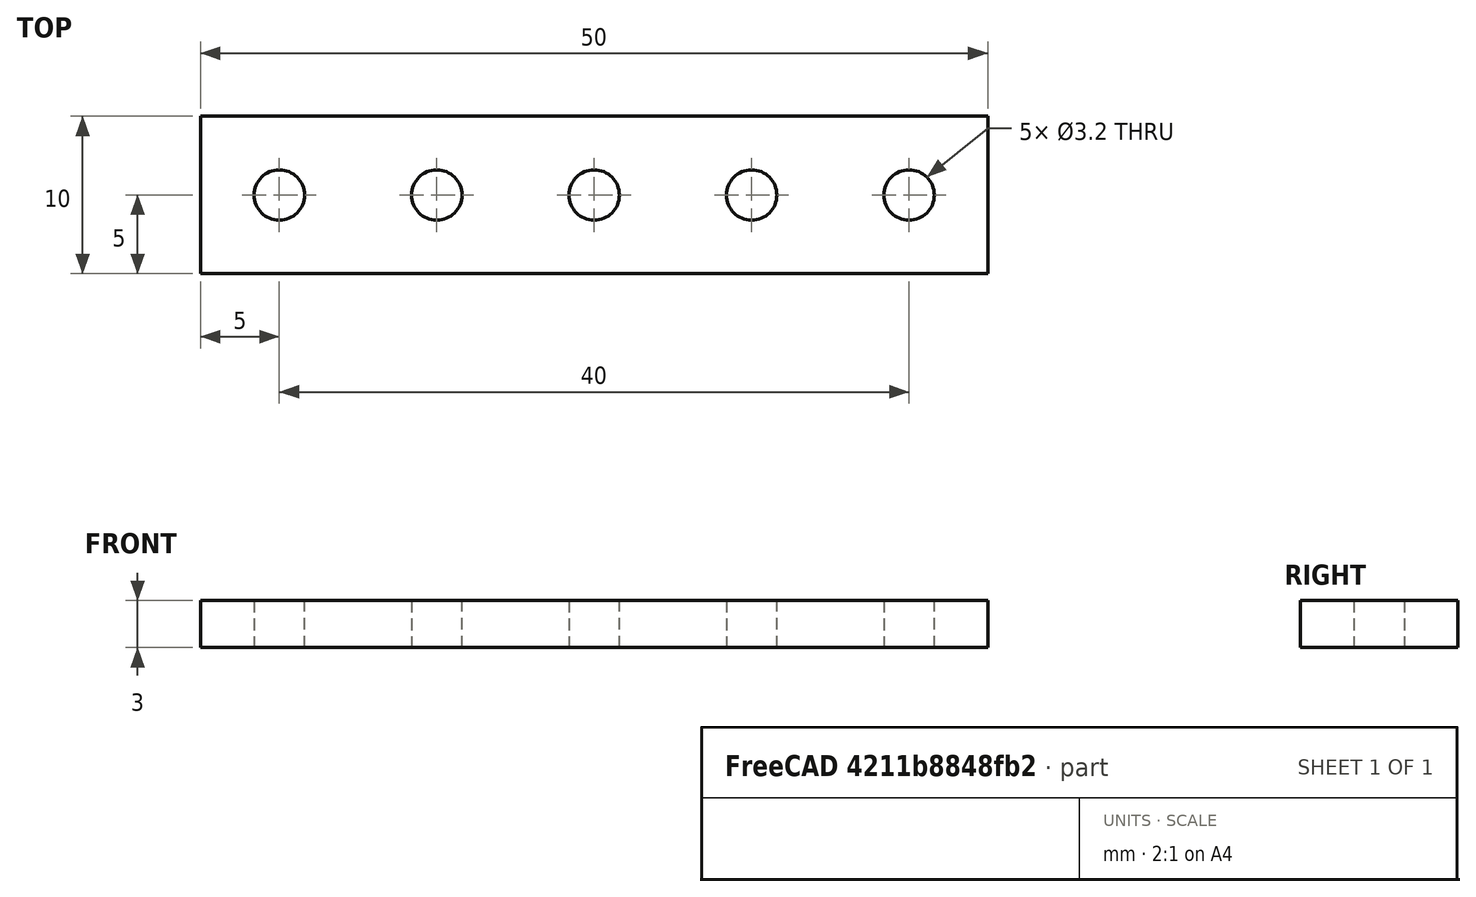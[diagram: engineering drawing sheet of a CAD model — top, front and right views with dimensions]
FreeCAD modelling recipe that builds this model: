
FCSTD DOCUMENT  (FreeCAD 1.0R38806 (Git))
Label: pieza
License: All rights reserved
LicenseURL: https://en.wikipedia.org/wiki/All_rights_reserved
objects: Part::Cylinder×5, App::FeaturePython×3, Part::Box×1, Part::MultiFuse×1, Part::Cut×1
note: 8 computed .brp shape members not serialized (recipe doc carries the construction recipe); baked Part::Feature solids carry a one-line shape summary decoded from their .brp

FEATURE [Part::Box] Box  label="Cube"
  AttacherType = Attacher::AttachEngine3D
  Height = 3
  Length = 50
  Width = 10
FEATURE [Part::Cylinder] Cylinder
  Angle = 360
  AttacherType = Attacher::AttachEngine3D
  FirstAngle = 0
  Height = 10
  Placement = pos=(5,5,-3) rot=(0,0,1;0rad)
  Radius = 1.6
  SecondAngle = 0
FEATURE [Part::Cylinder] Cylinder001 .. Cylinder004  x4 (patterned run collapsed; names and placements below)
  Angle = 360
  AttacherType = Attacher::AttachEngine3D
  FirstAngle = 0
  Height = 10
  Radius = 1.6
  SecondAngle = 0
  placements: 4 in arithmetic series — first pos=(15,5,-3) rot=(0,0,1;0rad), step (10,0,0), last pos=(45,5,-3) rot=(0,0,1;0rad)
FEATURE [Part::MultiFuse] Fusion
  Refine = true
  Shapes = -> [Cylinder004,Cylinder001,Cylinder,Cylinder002,Cylinder003]
FEATURE [Part::Cut] Cut
  Base = -> Box
  Refine = true
  Tool = -> Fusion
FEATURE [App::FeaturePython] Dimension  # Draft dimension (typed FeaturePython)
  Diameter = false
  Dimline = (0,10,3)
  Direction = (0,0,0)
  Distance = 10
  End = (0,10,3)
  Normal = (0,0,1)
  Start = (0,0,3)
FEATURE [App::FeaturePython] Dimension001  # Draft dimension (typed FeaturePython)
  Diameter = false
  Dimline = (50,10,3)
  Direction = (0,0,0)
  Distance = 50
  End = (50,10,3)
  Normal = (0,0,1)
  Start = (0,10,3)
FEATURE [App::FeaturePython] Dimension002  # Draft dimension (typed FeaturePython)
  Diameter = false
  Dimline = (50,10.3382,1.738)
  Direction = (0,0,0)
  Distance = 3
  End = (50,10,3)
  Normal = (1,0,0)
  Start = (50,10,0)
